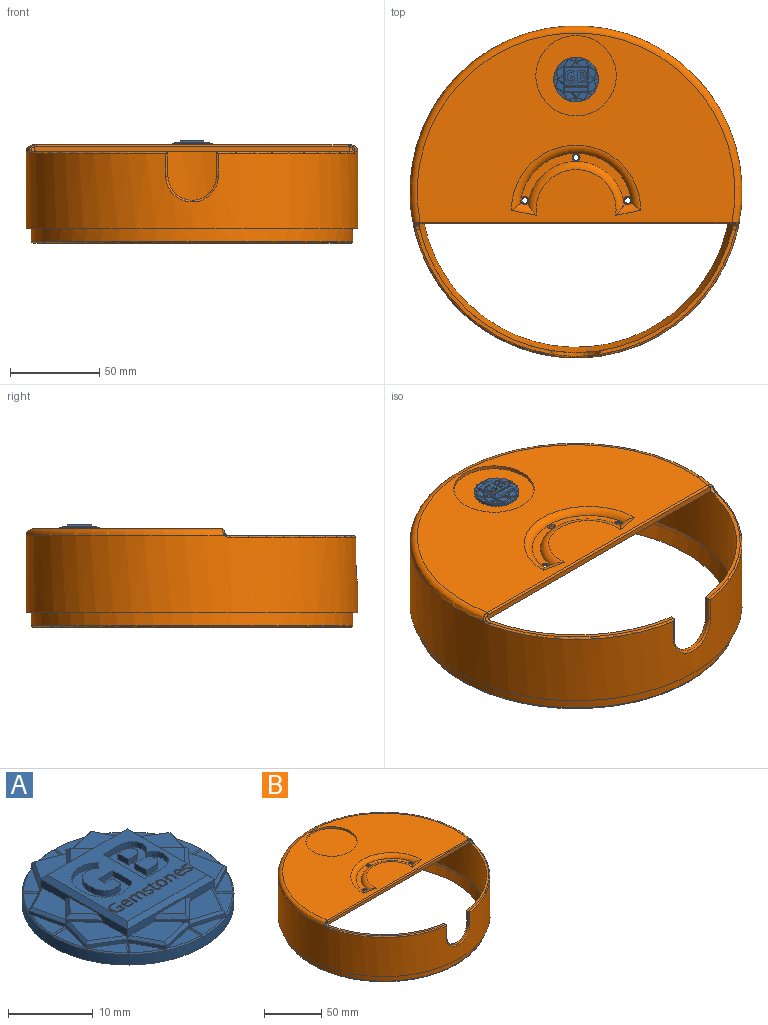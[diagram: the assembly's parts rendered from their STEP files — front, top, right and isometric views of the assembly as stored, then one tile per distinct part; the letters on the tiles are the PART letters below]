
ASSEMBLY  parts=2 mates=1
PART A: 356 faces, bbox 25.1x25.1x4.2 mm
  f0: plane 14.49x1.42mm, normal (0,1,0), area 11.4mm2, adj f11,f13,f15,f320,f322,f339,f340,f341
  f1: cylinder r=12.53mm len=25.05mm, axis (0,0,-1), area 118.3mm2, adj f3,f6,f270,f273,f281,f284,f287,f290
  f2: plane 4.16x4.14mm, normal (0,0,1), area 5.8mm2, adj f3,f4,f8
  f3: cone r=12.36mm half-angle=45deg, axis (0,0,-1), area 1.2mm2, adj f1,f2,f4,f8
  f4: plane 1.74x1.58mm, normal (-0.51,0.49,0.71), area 0.5mm2, adj f2,f3,f7,f8
  f5: plane 3.71x3.26mm, normal (0,0,1), area 4.4mm2, adj f6,f7,f344
  f6: cone r=12.36mm half-angle=45deg, axis (0,0,-1), area 1mm2, adj f1,f5,f7,f344
  f7: plane 1.65x1.65mm, normal (0.51,-0.49,0.71), area 0.5mm2, adj f4,f5,f6,f344
  f8: plane 4.54x2.88mm, normal (0.54,0.84,0), area 2.7mm2, adj f2,f3,f4,f261,f264,f344
  f9: plane 4.32x2.61mm, normal (-0.52,-0.86,0), area 2.6mm2, adj f297,f300,f328,f336,f337,f338
  f10: plane 14.49x1.42mm, normal (0,-1,0), area 11.2mm2, adj f11,f13,f16,f277,f279,f323,f324,f325
  f11: plane 14.55x1.42mm, normal (1,0,0), area 11.1mm2, adj f0,f10,f17,f257,f258,f260,f262,f264
  f12: plane 13.39x13.32mm, normal (0,0,1), area 117.2mm2, adj f14,f15,f16,f17,f18,f19,f20,f21
  f13: plane 14.55x1.42mm, normal (-1,0,0), area 11.1mm2, adj f0,f10,f14,f292,f293,f294,f295,f296
  f14: plane 14.55x0.58mm, normal (-0.71,0,0.71), area 11.5mm2, adj f12,f13,f15,f16
  f15: plane 14.49x0.58mm, normal (0,0.71,0.71), area 11.5mm2, adj f0,f12,f14,f17
  f16: plane 14.49x0.58mm, normal (0,-0.71,0.71), area 11.5mm2, adj f10,f12,f14,f17
  f17: plane 14.55x0.58mm, normal (0.71,0,0.71), area 11.5mm2, adj f11,f12,f15,f16
  f18: extruded ~3.58x3.34mm, area 4.6mm2, adj f12,f19,f31,f32
  f19: extruded ~2.26x0.84mm, area 2.1mm2, adj f12,f18,f20,f32
  f20: plane 3.14x0.84mm, normal (-1,0,0), area 2.6mm2, adj f12,f19,f21,f32
  f21: plane 2.48x0.84mm, normal (0,-1,0), area 2.1mm2, adj f12,f20,f22,f32
  f22: plane 1.14x0.84mm, normal (1,0,0), area 1mm2, adj f12,f21,f23,f32
  f23: plane 1.23x0.84mm, normal (0,1,0), area 1mm2, adj f12,f22,f24,f32
  f24: plane 1.37x0.84mm, normal (1,0,0), area 1.1mm2, adj f12,f23,f25,f32
  f25: extruded ~0.87x0.84mm, area 0.8mm2, adj f12,f24,f26,f32
  f26: extruded ~2.43x2.06mm, area 3mm2, adj f12,f25,f27,f32
  f27: extruded ~2.4x1.97mm, area 2.9mm2, adj f12,f26,f28,f32
  f28: extruded ~1.36x0.84mm, area 1.3mm2, adj f12,f27,f29,f32
  f29: plane 0.88x0.84mm, normal (-0.77,0.64,0), area 1mm2, adj f12,f28,f30,f32
  f30: extruded ~2.15x0.89mm, area 2mm2, adj f12,f29,f31,f32
  f31: extruded ~3.64x3.34mm, area 4.6mm2, adj f12,f18,f30,f32
  f32: plane 7.23x5.6mm, normal (0,0,1), area 21.4mm2, adj f18,f19,f20,f21,f22,f23,f24,f25
  f33: plane 6.96x0.84mm, normal (1,0,0), area 5.8mm2, adj f12,f34,f50,f51
  f34: plane 2.48x0.84mm, normal (0,1,0), area 2.1mm2, adj f12,f33,f35,f51
  f35: extruded ~2.7x2.05mm, area 3.2mm2, adj f12,f34,f36,f51
  f36: extruded ~1.65x1.31mm, area 1.9mm2, adj f12,f35,f37,f51
  f37: plane 0.84x0.05mm, normal (-1,0,0), area 0mm2, adj f12,f36,f38,f51
  f38: extruded ~1.51x0.95mm, area 1.6mm2, adj f12,f37,f39,f51
  f39: extruded ~2.52x1.71mm, area 2.9mm2, adj f12,f38,f50,f51
  f40: plane 0.97x0.84mm, normal (0,-1,0), area 0.8mm2, adj f41,f48,f51,f53
  f41: plane 2.02x0.84mm, normal (-1,0,0), area 1.7mm2, adj f40,f42,f51,f53
  f42: plane 0.97x0.84mm, normal (0,1,0), area 0.8mm2, adj f41,f43,f51,f53
  f43: extruded ~1.47x0.96mm, area 1.7mm2, adj f42,f48,f51,f53
  f44: plane 0.84x0.81mm, normal (0,-1,0), area 0.7mm2, adj f45,f49,f51,f52
  f45: plane 1.77x0.84mm, normal (-1,0,0), area 1.5mm2, adj f44,f46,f51,f52
  f46: plane 0.84x0.83mm, normal (0,1,0), area 0.7mm2, adj f45,f47,f51,f52
  f47: extruded ~1.25x0.86mm, area 1.4mm2, adj f46,f49,f51,f52
  f48: extruded ~1.47x1.06mm, area 1.7mm2, adj f40,f43,f51,f53
  f49: extruded ~1.27x0.91mm, area 1.5mm2, adj f44,f47,f51,f52
  f50: plane 2.3x0.84mm, normal (0,-1,0), area 1.9mm2, adj f12,f33,f39,f51
  f51: plane 6.96x5.18mm, normal (0,0,1), area 24.5mm2, adj f33,f34,f35,f36,f37,f38,f39,f40
  f52: plane 2.08x1.77mm, normal (0,0,1), area 3.3mm2, adj f44,f45,f46,f47,f49
  f53: plane 2.44x2.02mm, normal (0,0,1), area 4.4mm2, adj f40,f41,f42,f43,f48
  f54: extruded ~0.84x0.26mm, area 0.2mm2, adj f55,f72,f73,f252
  f55: extruded ~0.84x0.24mm, area 0.2mm2, adj f54,f56,f73,f252
  f56: extruded ~0.84x0.29mm, area 0.3mm2, adj f55,f57,f73,f252
  f57: plane 0.84x0.7mm, normal (0,-1,0), area 0.6mm2, adj f56,f72,f73,f252
  f58: extruded ~0.84x0.47mm, area 0.4mm2, adj f12,f59,f71,f73
  f59: extruded ~0.84x0.23mm, area 0.2mm2, adj f12,f58,f60,f73
  f60: extruded ~0.84x0.2mm, area 0.2mm2, adj f12,f59,f61,f73
  f61: plane 0.84x0.18mm, normal (-1,0,0), area 0.2mm2, adj f12,f60,f62,f73
  f62: extruded ~0.84x0.43mm, area 0.4mm2, adj f12,f61,f63,f73
  f63: extruded ~0.84x0.32mm, area 0.3mm2, adj f12,f62,f64,f73
  f64: extruded ~0.84x0.36mm, area 0.3mm2, adj f12,f63,f65,f73
  f65: plane 0.92x0.84mm, normal (0,1,0), area 0.8mm2, adj f12,f64,f66,f73
  f66: plane 0.84x0.13mm, normal (-1,0,0), area 0.1mm2, adj f12,f65,f67,f73
  f67: extruded ~0.84x0.44mm, area 0.4mm2, adj f12,f66,f68,f73
  f68: extruded ~0.84x0.4mm, area 0.4mm2, adj f12,f67,f69,f73
  f69: extruded ~0.84x0.43mm, area 0.4mm2, adj f12,f68,f70,f73
  f70: extruded ~0.84x0.51mm, area 0.5mm2, adj f12,f69,f71,f73
  f71: extruded ~0.84x0.5mm, area 0.5mm2, adj f12,f58,f70,f73
  f72: extruded ~0.84x0.29mm, area 0.3mm2, adj f54,f57,f73,f252
  f73: plane 1.39x1.13mm, normal (0,0,1), area 0.7mm2, adj f54,f55,f56,f57,f58,f59,f60,f61
  f74: plane 0.84x0.61mm, normal (0,-1,0), area 0.5mm2, adj f12,f75,f93,f94
  f75: plane 0.84x0.19mm, normal (1,0,0), area 0.2mm2, adj f12,f74,f76,f94
  f76: plane 0.84x0.4mm, normal (0,1,0), area 0.3mm2, adj f12,f75,f77,f94
  f77: plane 0.84x0.55mm, normal (1,0,0), area 0.5mm2, adj f12,f76,f78,f94
  f78: extruded ~0.84x0.36mm, area 0.3mm2, adj f12,f77,f79,f94
  f79: extruded ~0.84x0.52mm, area 0.5mm2, adj f12,f78,f80,f94
  f80: extruded ~0.84x0.55mm, area 0.5mm2, adj f12,f79,f81,f94
  f81: extruded ~0.84x0.54mm, area 0.5mm2, adj f12,f80,f82,f94
  f82: extruded ~0.84x0.51mm, area 0.5mm2, adj f12,f81,f83,f94
  f83: extruded ~0.84x0.46mm, area 0.4mm2, adj f12,f82,f84,f94
  f84: plane 0.84x0.18mm, normal (-0.92,0.4,0), area 0.2mm2, adj f12,f83,f85,f94
  f85: extruded ~0.84x0.53mm, area 0.5mm2, adj f12,f84,f86,f94
  f86: extruded ~0.84x0.49mm, area 0.4mm2, adj f12,f85,f87,f94
  f87: extruded ~0.84x0.32mm, area 0.4mm2, adj f12,f86,f88,f94
  f88: extruded ~0.84x0.49mm, area 0.4mm2, adj f12,f87,f89,f94
  f89: extruded ~0.84x0.67mm, area 0.6mm2, adj f12,f88,f90,f94
  f90: extruded ~0.84x0.63mm, area 0.6mm2, adj f12,f89,f91,f94
  f91: extruded ~0.84x0.34mm, area 0.3mm2, adj f12,f90,f92,f94
  f92: extruded ~0.84x0.29mm, area 0.2mm2, adj f12,f91,f93,f94
  f93: plane 0.87x0.84mm, normal (-1,0,0), area 0.7mm2, adj f12,f74,f92,f94
  f94: plane 1.83x1.48mm, normal (0,0,1), area 1mm2, adj f74,f75,f76,f77,f78,f79,f80,f81
  f95: plane 0.87x0.84mm, normal (1,0,0), area 0.7mm2, adj f12,f96,f122,f123
  f96: plane 0.84x0.2mm, normal (0,1,0), area 0.2mm2, adj f12,f95,f97,f123
  f97: plane 0.87x0.84mm, normal (-1,0,0), area 0.7mm2, adj f12,f96,f98,f123
  f98: extruded ~0.84x0.37mm, area 0.3mm2, adj f12,f97,f99,f123
  f99: extruded ~0.84x0.34mm, area 0.3mm2, adj f12,f98,f100,f123
  f100: extruded ~0.84x0.26mm, area 0.2mm2, adj f12,f99,f101,f123
  f101: extruded ~0.84x0.17mm, area 0.2mm2, adj f12,f100,f102,f123
  f102: plane 0.84x0.01mm, normal (0,-1,0), area 0mm2, adj f12,f101,f103,f123
  f103: extruded ~0.84x0.41mm, area 0.4mm2, adj f12,f102,f104,f123
  f104: extruded ~0.84x0.23mm, area 0.2mm2, adj f12,f103,f105,f123
  f105: extruded ~0.84x0.16mm, area 0.2mm2, adj f12,f104,f106,f123
  f106: plane 0.84x0.01mm, normal (0,-1,0), area 0mm2, adj f12,f105,f107,f123
  f107: plane 0.84x0.18mm, normal (-0.98,-0.18,0), area 0.2mm2, adj f12,f106,f108,f123
  f108: plane 0.84x0.16mm, normal (0,-1,0), area 0.1mm2, adj f12,f107,f109,f123
  f109: plane 1.34x0.84mm, normal (1,0,0), area 1.1mm2, adj f12,f108,f110,f123
  f110: plane 0.84x0.2mm, normal (0,1,0), area 0.2mm2, adj f12,f109,f111,f123
  f111: plane 0.84x0.7mm, normal (-1,0,0), area 0.6mm2, adj f12,f110,f112,f123
  f112: extruded ~0.84x0.37mm, area 0.3mm2, adj f12,f111,f113,f123
  f113: extruded ~0.84x0.28mm, area 0.3mm2, adj f12,f112,f114,f123
  f114: extruded ~0.84x0.21mm, area 0.2mm2, adj f12,f113,f115,f123
  f115: extruded ~0.84x0.24mm, area 0.2mm2, adj f12,f114,f116,f123
  f116: plane 0.87x0.84mm, normal (1,0,0), area 0.7mm2, adj f12,f115,f117,f123
  f117: plane 0.84x0.2mm, normal (0,1,0), area 0.2mm2, adj f12,f116,f118,f123
  f118: plane 0.84x0.75mm, normal (-1,0,0), area 0.6mm2, adj f12,f117,f119,f123
  f119: extruded ~0.84x0.33mm, area 0.3mm2, adj f12,f118,f120,f123
  f120: extruded ~0.84x0.28mm, area 0.3mm2, adj f12,f119,f121,f123
  f121: extruded ~0.84x0.21mm, area 0.2mm2, adj f12,f120,f122,f123
  f122: extruded ~0.84x0.24mm, area 0.2mm2, adj f12,f95,f121,f123
  f123: plane 1.91x1.36mm, normal (0,0,1), area 1mm2, adj f95,f96,f97,f98,f99,f100,f101,f102
  f124: extruded ~0.84x0.29mm, area 0.3mm2, adj f12,f125,f148,f149
  f125: extruded ~0.84x0.22mm, area 0.2mm2, adj f12,f124,f126,f149
  f126: extruded ~0.84x0.32mm, area 0.3mm2, adj f12,f125,f127,f149
  f127: extruded ~0.84x0.23mm, area 0.2mm2, adj f12,f126,f128,f149
  f128: extruded ~0.84x0.09mm, area 0.1mm2, adj f12,f127,f129,f149
  f129: extruded ~0.84x0.09mm, area 0.1mm2, adj f12,f128,f130,f149
  f130: extruded ~0.84x0.12mm, area 0.1mm2, adj f12,f129,f131,f149
  f131: extruded ~0.84x0.22mm, area 0.2mm2, adj f12,f130,f132,f149
  f132: extruded ~0.84x0.36mm, area 0.3mm2, adj f12,f131,f133,f149
  f133: plane 0.84x0.16mm, normal (-0.92,0.4,0), area 0.2mm2, adj f12,f132,f134,f149
  f134: extruded ~0.84x0.42mm, area 0.4mm2, adj f12,f133,f135,f149
  f135: extruded ~0.84x0.36mm, area 0.3mm2, adj f12,f134,f136,f149
  f136: extruded ~0.84x0.26mm, area 0.3mm2, adj f12,f135,f137,f149
  f137: extruded ~0.84x0.16mm, area 0.1mm2, adj f12,f136,f138,f149
  f138: extruded ~0.84x0.12mm, area 0.1mm2, adj f12,f137,f139,f149
  f139: extruded ~0.84x0.27mm, area 0.2mm2, adj f12,f138,f140,f149
  f140: extruded ~0.84x0.26mm, area 0.2mm2, adj f12,f139,f141,f149
  f141: extruded ~0.84x0.13mm, area 0.1mm2, adj f12,f140,f142,f149
  f142: extruded ~0.84x0.15mm, area 0.2mm2, adj f12,f141,f143,f149
  f143: extruded ~0.84x0.24mm, area 0.2mm2, adj f12,f142,f144,f149
  f144: extruded ~0.84x0.21mm, area 0.2mm2, adj f12,f143,f145,f149
  f145: extruded ~0.84x0.21mm, area 0.2mm2, adj f12,f144,f146,f149
  f146: plane 0.84x0.19mm, normal (1,0,0), area 0.2mm2, adj f12,f145,f147,f149
  f147: extruded ~0.84x0.41mm, area 0.4mm2, adj f12,f146,f148,f149
  f148: extruded ~0.84x0.39mm, area 0.3mm2, adj f12,f124,f147,f149
  f149: plane 1.39x0.95mm, normal (0,0,1), area 0.5mm2, adj f124,f125,f126,f127,f128,f129,f130,f131
  f150: extruded ~0.84x0.1mm, area 0.1mm2, adj f12,f151,f168,f169
  f151: extruded ~0.84x0.16mm, area 0.1mm2, adj f12,f150,f152,f169
  f152: extruded ~0.84x0.19mm, area 0.2mm2, adj f12,f151,f153,f169
  f153: plane 0.84x0.79mm, normal (-1,0,0), area 0.7mm2, adj f12,f152,f154,f169
  f154: plane 0.84x0.39mm, normal (0,1,0), area 0.3mm2, adj f12,f153,f155,f169
  f155: plane 0.84x0.16mm, normal (-1,0,0), area 0.1mm2, adj f12,f154,f156,f169
  f156: plane 0.84x0.39mm, normal (0,-1,0), area 0.3mm2, adj f12,f155,f157,f169
  f157: plane 0.84x0.31mm, normal (-1,0,0), area 0.3mm2, adj f12,f156,f158,f169
  f158: plane 0.84x0.12mm, normal (0,-1,0), area 0.1mm2, adj f12,f157,f159,f169
  f159: plane 0.84x0.29mm, normal (0.96,-0.29,0), area 0.2mm2, adj f12,f158,f160,f169
  f160: plane 0.84x0.19mm, normal (0.4,-0.92,0), area 0.2mm2, adj f12,f159,f161,f169
  f161: plane 0.84x0.1mm, normal (1,0,0), area 0.1mm2, adj f12,f160,f162,f169
  f162: plane 0.84x0.19mm, normal (0,1,0), area 0.2mm2, adj f12,f161,f163,f169
  f163: plane 0.84x0.8mm, normal (1,0,0), area 0.7mm2, adj f12,f162,f164,f169
  f164: extruded ~0.84x0.41mm, area 0.5mm2, adj f12,f163,f165,f169
  f165: extruded ~0.84x0.12mm, area 0.1mm2, adj f12,f164,f166,f169
  f166: extruded ~0.84x0.1mm, area 0.1mm2, adj f12,f165,f167,f169
  f167: plane 0.84x0.16mm, normal (-1,0,0), area 0.1mm2, adj f12,f166,f168,f169
  f168: extruded ~0.84x0.08mm, area 0.1mm2, adj f12,f150,f167,f169
  f169: plane 1.67x0.79mm, normal (0,0,1), area 0.5mm2, adj f150,f151,f152,f153,f154,f155,f156,f157
  f170: plane 0.86x0.84mm, normal (1,0,0), area 0.7mm2, adj f12,f171,f186,f187
  f171: plane 0.84x0.2mm, normal (0,1,0), area 0.2mm2, adj f12,f170,f172,f187
  f172: plane 0.87x0.84mm, normal (-1,0,0), area 0.7mm2, adj f12,f171,f173,f187
  f173: extruded ~0.84x0.37mm, area 0.3mm2, adj f12,f172,f174,f187
  f174: extruded ~0.84x0.36mm, area 0.3mm2, adj f12,f173,f175,f187
  f175: extruded ~0.84x0.25mm, area 0.2mm2, adj f12,f174,f176,f187
  f176: extruded ~0.84x0.17mm, area 0.2mm2, adj f12,f175,f177,f187
  f177: plane 0.84x0.01mm, normal (0,-1,0), area 0mm2, adj f12,f176,f178,f187
  f178: plane 0.84x0.18mm, normal (-0.98,-0.18,0), area 0.2mm2, adj f12,f177,f179,f187
  f179: plane 0.84x0.16mm, normal (0,-1,0), area 0.1mm2, adj f12,f178,f180,f187
  f180: plane 1.34x0.84mm, normal (1,0,0), area 1.1mm2, adj f12,f179,f181,f187
  f181: plane 0.84x0.2mm, normal (0,1,0), area 0.2mm2, adj f12,f180,f182,f187
  f182: plane 0.84x0.7mm, normal (-1,0,0), area 0.6mm2, adj f12,f181,f183,f187
  f183: extruded ~0.84x0.37mm, area 0.3mm2, adj f12,f182,f184,f187
  f184: extruded ~0.84x0.31mm, area 0.3mm2, adj f12,f183,f185,f187
  f185: extruded ~0.84x0.23mm, area 0.2mm2, adj f12,f184,f186,f187
  f186: extruded ~0.84x0.24mm, area 0.2mm2, adj f12,f170,f185,f187
  f187: plane 1.36x1.12mm, normal (0,0,1), area 0.6mm2, adj f170,f171,f172,f173,f174,f175,f176,f177
  f188: extruded ~0.84x0.29mm, area 0.3mm2, adj f12,f189,f212,f213
  f189: extruded ~0.84x0.22mm, area 0.2mm2, adj f12,f188,f190,f213
  f190: extruded ~0.84x0.32mm, area 0.3mm2, adj f12,f189,f191,f213
  f191: extruded ~0.84x0.23mm, area 0.2mm2, adj f12,f190,f192,f213
  f192: extruded ~0.84x0.09mm, area 0.1mm2, adj f12,f191,f193,f213
  f193: extruded ~0.84x0.09mm, area 0.1mm2, adj f12,f192,f194,f213
  f194: extruded ~0.84x0.12mm, area 0.1mm2, adj f12,f193,f195,f213
  f195: extruded ~0.84x0.22mm, area 0.2mm2, adj f12,f194,f196,f213
  f196: extruded ~0.84x0.36mm, area 0.3mm2, adj f12,f195,f197,f213
  f197: plane 0.84x0.16mm, normal (-0.92,0.4,0), area 0.2mm2, adj f12,f196,f198,f213
  f198: extruded ~0.84x0.42mm, area 0.4mm2, adj f12,f197,f199,f213
  f199: extruded ~0.84x0.36mm, area 0.3mm2, adj f12,f198,f200,f213
  f200: extruded ~0.84x0.26mm, area 0.3mm2, adj f12,f199,f201,f213
  f201: extruded ~0.84x0.16mm, area 0.1mm2, adj f12,f200,f202,f213
  f202: extruded ~0.84x0.12mm, area 0.1mm2, adj f12,f201,f203,f213
  f203: extruded ~0.84x0.27mm, area 0.2mm2, adj f12,f202,f204,f213
  f204: extruded ~0.84x0.26mm, area 0.2mm2, adj f12,f203,f205,f213
  f205: extruded ~0.84x0.13mm, area 0.1mm2, adj f12,f204,f206,f213
  f206: extruded ~0.84x0.15mm, area 0.2mm2, adj f12,f205,f207,f213
  f207: extruded ~0.84x0.24mm, area 0.2mm2, adj f12,f206,f208,f213
  f208: extruded ~0.84x0.21mm, area 0.2mm2, adj f12,f207,f209,f213
  f209: extruded ~0.84x0.21mm, area 0.2mm2, adj f12,f208,f210,f213
  f210: plane 0.84x0.19mm, normal (1,0,0), area 0.2mm2, adj f12,f209,f211,f213
  f211: extruded ~0.84x0.41mm, area 0.4mm2, adj f12,f210,f212,f213
  f212: extruded ~0.84x0.39mm, area 0.3mm2, adj f12,f188,f211,f213
  f213: plane 1.39x0.95mm, normal (0,0,1), area 0.5mm2, adj f188,f189,f190,f191,f192,f193,f194,f195
  f214: extruded ~0.84x0.26mm, area 0.2mm2, adj f215,f232,f233,f253
  f215: extruded ~0.84x0.24mm, area 0.2mm2, adj f214,f216,f233,f253
  f216: extruded ~0.84x0.29mm, area 0.3mm2, adj f215,f217,f233,f253
  f217: plane 0.84x0.7mm, normal (0,-1,0), area 0.6mm2, adj f216,f232,f233,f253
  f218: extruded ~0.84x0.47mm, area 0.4mm2, adj f12,f219,f231,f233
  f219: extruded ~0.84x0.23mm, area 0.2mm2, adj f12,f218,f220,f233
  f220: extruded ~0.84x0.2mm, area 0.2mm2, adj f12,f219,f221,f233
  f221: plane 0.84x0.18mm, normal (-1,0,0), area 0.2mm2, adj f12,f220,f222,f233
  f222: extruded ~0.84x0.43mm, area 0.4mm2, adj f12,f221,f223,f233
  f223: extruded ~0.84x0.32mm, area 0.3mm2, adj f12,f222,f224,f233
  f224: extruded ~0.84x0.36mm, area 0.3mm2, adj f12,f223,f225,f233
  f225: plane 0.92x0.84mm, normal (0,1,0), area 0.8mm2, adj f12,f224,f226,f233
  f226: plane 0.84x0.13mm, normal (-1,0,0), area 0.1mm2, adj f12,f225,f227,f233
  f227: extruded ~0.84x0.44mm, area 0.4mm2, adj f12,f226,f228,f233
  f228: extruded ~0.84x0.4mm, area 0.4mm2, adj f12,f227,f229,f233
  f229: extruded ~0.84x0.43mm, area 0.4mm2, adj f12,f228,f230,f233
  f230: extruded ~0.84x0.51mm, area 0.5mm2, adj f12,f229,f231,f233
  f231: extruded ~0.84x0.5mm, area 0.5mm2, adj f12,f218,f230,f233
  f232: extruded ~0.84x0.29mm, area 0.3mm2, adj f214,f217,f233,f253
  f233: plane 1.39x1.13mm, normal (0,0,1), area 0.7mm2, adj f214,f215,f216,f217,f218,f219,f220,f221
  f234: extruded ~0.84x0.39mm, area 0.3mm2, adj f235,f250,f251,f254
  f235: extruded ~0.84x0.39mm, area 0.3mm2, adj f234,f236,f251,f254
  f236: extruded ~0.84x0.3mm, area 0.3mm2, adj f235,f237,f251,f254
  f237: extruded ~0.84x0.3mm, area 0.3mm2, adj f236,f238,f251,f254
  f238: extruded ~0.84x0.39mm, area 0.3mm2, adj f237,f239,f251,f254
  f239: extruded ~0.84x0.39mm, area 0.3mm2, adj f238,f240,f251,f254
  f240: extruded ~0.84x0.3mm, area 0.3mm2, adj f239,f250,f251,f254
  f241: extruded ~0.84x0.51mm, area 0.5mm2, adj f12,f242,f249,f251
  f242: extruded ~0.84x0.5mm, area 0.5mm2, adj f12,f241,f243,f251
  f243: extruded ~0.84x0.45mm, area 0.4mm2, adj f12,f242,f244,f251
  f244: extruded ~0.84x0.45mm, area 0.4mm2, adj f12,f243,f245,f251
  f245: extruded ~0.84x0.51mm, area 0.5mm2, adj f12,f244,f246,f251
  f246: extruded ~0.84x0.37mm, area 0.3mm2, adj f12,f245,f247,f251
  f247: extruded ~0.84x0.24mm, area 0.3mm2, adj f12,f246,f248,f251
  f248: extruded ~0.84x0.32mm, area 0.3mm2, adj f12,f247,f249,f251
  f249: extruded ~0.84x0.45mm, area 0.4mm2, adj f12,f241,f248,f251
  f250: extruded ~0.84x0.3mm, area 0.3mm2, adj f234,f240,f251,f254
  f251: plane 1.39x1.23mm, normal (0,0,1), area 0.7mm2, adj f234,f235,f236,f237,f238,f239,f240,f241
  f252: plane 0.7x0.39mm, normal (0,0,1), area 0.2mm2, adj f54,f55,f56,f57,f72
  f253: plane 0.7x0.39mm, normal (0,0,1), area 0.2mm2, adj f214,f215,f216,f217,f232
  f254: plane 1.04x0.81mm, normal (0,0,1), area 0.7mm2, adj f234,f235,f236,f237,f238,f239,f240,f250
  f255: plane 4.27x2.15mm, normal (0.45,-0.89,0), area 2.4mm2, adj f256,f258,f275,f289,f290,f291
  f256: plane 5.21x1.18mm, normal (0.98,0.22,0), area 2.7mm2, adj f255,f259,f261,f272,f273,f274
  f257: plane 6.7x3.88mm, normal (0,0,1), area 15.6mm2, adj f11,f258,f259,f260
  f258: plane 4.27x2.33mm, normal (0.32,-0.63,0.71), area 2.2mm2, adj f11,f255,f257,f259
  f259: plane 5.21x1.46mm, normal (0.69,0.16,0.71), area 2.4mm2, adj f256,f257,f258,f260
  f260: plane 3.17x3.09mm, normal (0.72,-0.7,0), area 1.5mm2, adj f11,f257,f259,f265,f267
  f261: plane 4.33x1.45mm, normal (0.95,-0.32,0), area 2.3mm2, adj f8,f256,f263,f269,f270,f271
  f262: plane 6.55x4.14mm, normal (0,0,1), area 15.2mm2, adj f11,f263,f264,f265
  f263: plane 4.32x1.72mm, normal (0.67,-0.22,0.71), area 2.1mm2, adj f261,f262,f264,f265
  f264: plane 4.54x3.02mm, normal (0.38,0.6,0.71), area 2.4mm2, adj f8,f11,f262,f263
  f265: plane 3.09x3.01mm, normal (0.7,0.72,0), area 1.5mm2, adj f11,f260,f262,f263,f268
  f266: plane 4.76x2.38mm, normal (0,0,1), area 5.7mm2, adj f11,f267,f268
  f267: plane 3.17x3.09mm, normal (0.51,-0.49,0.71), area 2.8mm2, adj f11,f260,f266,f268
  f268: plane 3.09x3.02mm, normal (0.49,0.51,0.71), area 2.7mm2, adj f11,f265,f266,f267
  f269: plane 4.01x2.04mm, normal (0,0,1), area 4.5mm2, adj f261,f270,f271
  f270: cone r=12.36mm half-angle=45deg, axis (0,0,-1), area 1mm2, adj f1,f261,f269,f271
  f271: plane 2.26x0.28mm, normal (-0.03,-0.71,0.71), area 0.5mm2, adj f261,f269,f270,f274
  f272: plane 4.76x2.06mm, normal (0,0,1), area 5.6mm2, adj f256,f273,f274
  f273: cone r=12.36mm half-angle=45deg, axis (0,0,-1), area 1.2mm2, adj f1,f256,f272,f274
  f274: plane 2.26x0.27mm, normal (0.03,0.71,0.71), area 0.5mm2, adj f256,f271,f272,f273
  f275: plane 4.42x2.6mm, normal (0.86,-0.51,0), area 2.6mm2, adj f255,f276,f279,f286,f287,f288
  f276: plane 4.62x1.4mm, normal (-0.29,-0.96,0), area 2.5mm2, adj f275,f278,f283,f284,f285,f329
  f277: plane 6.54x4.02mm, normal (0,0,1), area 14.9mm2, adj f10,f278,f279,f326
  f278: plane 4.61x1.66mm, normal (-0.2,-0.68,0.71), area 2.2mm2, adj f276,f277,f279,f326
  f279: plane 4.42x2.75mm, normal (0.61,-0.36,0.71), area 2.3mm2, adj f10,f275,f277,f278
  f280: plane 4.65x2.05mm, normal (0,0,1), area 5.5mm2, adj f281,f282,f329
  f281: cone r=12.36mm half-angle=45deg, axis (0,0,-1), area 1.2mm2, adj f1,f280,f282,f329
  f282: plane 2.26x0.2mm, normal (0.71,0.01,0.71), area 0.5mm2, adj f280,f281,f285,f329
  f283: plane 4.18x2.04mm, normal (0,0,1), area 4.8mm2, adj f276,f284,f285
  f284: cone r=12.36mm half-angle=45deg, axis (0,0,-1), area 1.1mm2, adj f1,f276,f283,f285
  f285: plane 2.26x0.2mm, normal (-0.71,-0.01,0.71), area 0.5mm2, adj f276,f282,f283,f284
  f286: plane 4.03x3.9mm, normal (0,0,1), area 5.5mm2, adj f275,f287,f288
  f287: cone r=12.36mm half-angle=45deg, axis (0,0,-1), area 1.2mm2, adj f1,f275,f286,f288
  f288: plane 1.77x1.62mm, normal (0.49,0.51,0.71), area 0.5mm2, adj f275,f286,f287,f291
  f289: plane 3.87x3.41mm, normal (0,0,1), area 4.8mm2, adj f255,f290,f291
  f290: cone r=12.36mm half-angle=45deg, axis (0,0,-1), area 1mm2, adj f1,f255,f289,f291
  f291: plane 1.7x1.68mm, normal (-0.49,-0.51,0.71), area 0.5mm2, adj f255,f288,f289,f290
  f292: plane 3.02x2.95mm, normal (-0.71,0.7,0), area 1.5mm2, adj f13,f293,f295,f309,f311
  f293: plane 3.19x2.95mm, normal (-0.73,-0.68,0), area 1.5mm2, adj f13,f292,f296,f298,f299
  f294: plane 4.75x2.26mm, normal (0,0,1), area 5.4mm2, adj f13,f295,f296
  f295: plane 3.03x2.95mm, normal (-0.51,0.49,0.71), area 2.6mm2, adj f13,f292,f294,f296
  f296: plane 3.19x2.95mm, normal (-0.52,-0.48,0.71), area 2.7mm2, adj f13,f293,f294,f295
  f297: plane 4.75x1.37mm, normal (-0.96,0.28,0), area 2.5mm2, adj f9,f299,f308,f315,f316,f317
  f298: plane 6.68x3.93mm, normal (0,0,1), area 15mm2, adj f13,f293,f299,f300
  f299: plane 4.75x1.64mm, normal (-0.68,0.2,0.71), area 2.2mm2, adj f293,f297,f298,f300
  f300: plane 4.32x2.76mm, normal (-0.36,-0.61,0.71), area 2.3mm2, adj f9,f13,f298,f299
  f301: plane 4.16x4.05mm, normal (0,0,1), area 5.6mm2, adj f302,f303,f319
  f302: cone r=12.36mm half-angle=45deg, axis (0,0,-1), area 1.2mm2, adj f1,f301,f303,f319
  f303: plane 1.71x1.48mm, normal (-0.48,-0.52,0.71), area 0.5mm2, adj f301,f302,f306,f319
  f304: plane 3.71x3.29mm, normal (0,0,1), area 4.3mm2, adj f305,f306,f307
  f305: cone r=12.36mm half-angle=45deg, axis (0,0,-1), area 1mm2, adj f1,f304,f306,f307
  f306: plane 1.62x1.56mm, normal (0.48,0.52,0.71), area 0.5mm2, adj f303,f304,f305,f307
  f307: plane 4.11x2.17mm, normal (-0.47,0.88,0), area 2.4mm2, adj f304,f305,f306,f308,f310,f319
  f308: plane 5.03x1.16mm, normal (-0.97,-0.22,0), area 2.6mm2, adj f297,f307,f311,f312,f313,f314
  f309: plane 6.54x3.73mm, normal (0,0,1), area 14.6mm2, adj f13,f292,f310,f311
  f310: plane 4.11x2.35mm, normal (-0.33,0.63,0.71), area 2.1mm2, adj f13,f307,f309,f311
  f311: plane 5.03x1.44mm, normal (-0.69,-0.16,0.71), area 2.3mm2, adj f292,f308,f309,f310
  f312: plane 4.59x2.05mm, normal (0,0,1), area 5.4mm2, adj f308,f313,f314
  f313: cone r=12.36mm half-angle=45deg, axis (0,0,-1), area 1.2mm2, adj f1,f308,f312,f314
  f314: plane 2.26x0.17mm, normal (0,-0.71,0.71), area 0.5mm2, adj f308,f312,f313,f317
  f315: plane 4.32x2.05mm, normal (0,0,1), area 5mm2, adj f297,f316,f317
  f316: cone r=12.36mm half-angle=45deg, axis (0,0,-1), area 1.1mm2, adj f1,f297,f315,f317
  f317: plane 2.26x0.17mm, normal (0,0.71,0.71), area 0.5mm2, adj f297,f314,f315,f316
  f318: plane 4.19x1.55mm, normal (0.35,0.94,0), area 2.3mm2, adj f319,f321,f348,f349,f350,f351
  f319: plane 4.43x2.95mm, normal (-0.83,0.55,0), area 2.7mm2, adj f301,f302,f303,f307,f318,f322
  f320: plane 6.49x4.02mm, normal (0,0,1), area 14.8mm2, adj f0,f321,f322,f343
  f321: plane 4.19x1.81mm, normal (0.24,0.66,0.71), area 2mm2, adj f318,f320,f322,f343
  f322: plane 4.43x3.08mm, normal (-0.59,0.39,0.71), area 2.4mm2, adj f0,f319,f320,f321
  f323: plane 3.16x3.02mm, normal (0.49,-0.51,0.71), area 2.7mm2, adj f10,f324,f325,f326
  f324: plane 3.02x2.91mm, normal (-0.51,-0.49,0.71), area 2.6mm2, adj f10,f323,f325,f327
  f325: plane 4.63x2.31mm, normal (0,0,1), area 5.4mm2, adj f10,f323,f324
  f326: plane 3.16x3.02mm, normal (0.69,-0.72,0), area 1.5mm2, adj f10,f277,f278,f323,f327
  f327: plane 3.02x2.89mm, normal (-0.72,-0.69,0), area 1.5mm2, adj f10,f324,f326,f330,f332
  f328: plane 4.2x2.22mm, normal (-0.88,-0.47,0), area 2.4mm2, adj f9,f329,f331,f333,f334,f335
  f329: plane 5.06x1.18mm, normal (0.23,-0.97,0), area 2.6mm2, adj f276,f280,f281,f282,f328,f332
  f330: plane 6.63x3.81mm, normal (0,0,1), area 15.4mm2, adj f10,f327,f331,f332
  f331: plane 4.2x2.39mm, normal (-0.63,-0.33,0.71), area 2.1mm2, adj f10,f328,f330,f332
  f332: plane 5.06x1.46mm, normal (0.16,-0.69,0.71), area 2.3mm2, adj f327,f329,f330,f331
  f333: plane 3.8x3.33mm, normal (0,0,1), area 4.5mm2, adj f328,f334,f335
  f334: cone r=12.36mm half-angle=45deg, axis (0,0,-1), area 1mm2, adj f1,f328,f333,f335
  f335: plane 1.69x1.56mm, normal (-0.53,0.46,0.71), area 0.5mm2, adj f328,f333,f334,f338
  f336: plane 3.94x3.9mm, normal (0,0,1), area 5.3mm2, adj f9,f337,f338
  f337: cone r=12.36mm half-angle=45deg, axis (0,0,-1), area 1.2mm2, adj f1,f9,f336,f338
  f338: plane 1.77x1.48mm, normal (0.53,-0.46,0.71), area 0.5mm2, adj f9,f335,f336,f337
  f339: plane 2.88x2.76mm, normal (-0.51,0.49,0.71), area 2.5mm2, adj f0,f340,f341,f343
  f340: plane 3.03x2.88mm, normal (0.49,0.51,0.71), area 2.6mm2, adj f0,f339,f341,f342
  f341: plane 4.36x2.18mm, normal (0,0,1), area 4.7mm2, adj f0,f339,f340
  f342: plane 3.03x2.88mm, normal (0.69,0.72,0), area 1.5mm2, adj f0,f340,f343,f352,f354
  f343: plane 2.88x2.75mm, normal (-0.72,0.69,0), area 1.4mm2, adj f0,f320,f321,f339,f342
  f344: plane 4.11x2.04mm, normal (0.9,0.44,0), area 2.3mm2, adj f5,f6,f7,f8,f351,f353
  f345: plane 4.87x2.12mm, normal (0,0,1), area 5.8mm2, adj f346,f347,f351
  f346: cone r=12.36mm half-angle=45deg, axis (0,0,-1), area 1.2mm2, adj f1,f345,f347,f351
  f347: plane 2.33x0.33mm, normal (-0.71,0.05,0.71), area 0.5mm2, adj f345,f346,f350,f351
  f348: plane 3.94x2.1mm, normal (0,0,1), area 4.5mm2, adj f318,f349,f350
  f349: cone r=12.36mm half-angle=45deg, axis (0,0,-1), area 1mm2, adj f1,f318,f348,f350
  f350: plane 2.33x0.34mm, normal (0.71,-0.05,0.71), area 0.5mm2, adj f318,f347,f348,f349
  f351: plane 5.31x1.23mm, normal (-0.23,0.97,0), area 2.8mm2, adj f318,f344,f345,f346,f347,f354
  f352: plane 6.68x3.73mm, normal (0,0,1), area 15.2mm2, adj f0,f342,f353,f354
  f353: plane 4.11x2.22mm, normal (0.63,0.31,0.71), area 2.1mm2, adj f0,f344,f352,f354
  f354: plane 5.31x1.5mm, normal (-0.16,0.69,0.71), area 2.5mm2, adj f342,f351,f352,f353
  f355: plane 25.05x25.05mm, normal (0,0,-1), area 492.8mm2, adj f1
PART B: 41 faces, bbox 201.3x200.2x55 mm
  f0: plane 76.07x70mm, normal (0,0,1), area 216.4mm2, adj f17,f26,f30,f32,f34
  f1: plane 76.07x70mm, normal (0,0,1), area 216.4mm2, adj f17,f27,f29,f33,f35
  f2: cylinder r=93mm len=186mm, axis (0,0,1), area 24171.6mm2, adj f6,f25,f31,f32,f33,f34,f35,f36
  f3: plane 178x106mm, normal (0,0,1), area 12548.3mm2, adj f10,f11,f12,f13,f14,f25,f40
  f4: plane 178x178mm, normal (0,0,-1), area 1105.8mm2, adj f7,f18
  f5: cylinder r=90mm len=180mm, axis (0,0,-1), area 3958.4mm2, adj f6,f7
  f6: plane 186x186mm, normal (0,0,-1), area 1724.7mm2, adj f2,f5
  f7: torus R=89mm, axis (0,0,1), area 884.7mm2, adj f4,f5
  f8: plane 45x45mm, normal (0,0,1), area 1590.4mm2, adj f10
  f9: plane 62.76x29.13mm, normal (0,0,1), area 347.2mm2, adj f11,f12,f13,f14,f22,f23,f24
  f10: cylinder r=22.5mm len=45mm, axis (0,0,1), area 282.7mm2, adj f3,f8
  f11: torus R=22.42mm, axis (0,0,-1), area 462.1mm2, adj f3,f9,f12,f14
  f12: cylinder r=5mm len=14.87mm, axis (-0.98,-0.2,0), area 54.5mm2, adj f3,f9,f11,f13
  f13: torus R=36.14mm, axis (0,0,1), area 592.8mm2, adj f3,f9,f12,f14
  f14: cylinder r=5mm len=14.87mm, axis (0.98,-0.2,0), area 54.5mm2, adj f3,f9,f11,f13
  f15: plane 176.38x3.01mm, normal (0,-1,0), area 529.1mm2, adj f16,f17,f38,f39,f40
  f16: plane 180x108mm, normal (0,0,-1), area 15917.6mm2, adj f15,f17,f19,f20,f21
  f17: cylinder r=90mm len=180mm, axis (0,0,1), area 22536mm2, adj f0,f1,f15,f16,f18,f26,f27,f28
  f18: cone r=90mm half-angle=16.7deg, axis (0,0,1), area 5805.5mm2, adj f4,f17
  f19: cylinder r=1.6mm len=3.2mm, axis (0,0,1), area 4mm2, adj f16,f22
  f20: cylinder r=1.6mm len=3.2mm, axis (0,0,1), area 4mm2, adj f16,f24
  f21: cylinder r=1.6mm len=3.2mm, axis (0,0,1), area 4mm2, adj f16,f23
  f22: cone r=1.6mm half-angle=45deg, axis (0,0,1), area 10.1mm2, adj f9,f19
  f23: cone r=1.6mm half-angle=45deg, axis (0,0,1), area 10.1mm2, adj f9,f21
  f24: cone r=1.6mm half-angle=45deg, axis (0,0,1), area 10.1mm2, adj f9,f20
  f25: torus R=89mm, axis (0,0,1), area 2027mm2, adj f2,f3,f38,f39
  f26: plane 13.5x1.87mm, normal (1,0,0), area 25.2mm2, adj f0,f17,f28,f32
  f27: plane 13.5x1.87mm, normal (-1,0,0), area 25.2mm2, adj f1,f17,f28,f33
  f28: cylinder r=13.5mm len=27mm, axis (0,-1,0), area 82mm2, adj f17,f26,f27,f31
  f29: cylinder r=3mm len=3mm, axis (-1,0,0), area 7.6mm2, adj f1,f17,f37,f39
  f30: cylinder r=3mm len=3mm, axis (-1,0,0), area 7.6mm2, adj f0,f17,f36,f38
  f31: bspline ~29.32x16.12mm, area 72.1mm2, adj f2,f28,f32,f33
  f32: cylinder r=1mm len=13.5mm, axis (0,0,1), area 22.8mm2, adj f0,f2,f26,f31,f34
  f33: cylinder r=1mm len=13.5mm, axis (0,0,1), area 22.8mm2, adj f1,f2,f27,f31,f35
  f34: torus R=92mm, axis (0,0,1), area 172.8mm2, adj f0,f2,f32,f36
  f35: torus R=92mm, axis (0,0,1), area 172.8mm2, adj f1,f2,f33,f37
  f36: bspline ~4.14x2.17mm, area 3.8mm2, adj f2,f30,f34,f38
  f37: bspline ~4.14x2.17mm, area 3.8mm2, adj f2,f29,f35,f39
  f38: bspline ~4.47x4.23mm, area 7.5mm2, adj f15,f17,f25,f30,f36,f40
  f39: bspline ~4.6x4.22mm, area 7.5mm2, adj f15,f17,f25,f29,f37,f40
  f40: cylinder r=1mm len=174.72mm, axis (1,0,0), area 274.5mm2, adj f3,f15,f38,f39
PLACE A t=(1.88,66.55,28.86)mm
PLACE B t=(1.88,3.66,-24.14)mm
MATE parallel A.f1 <-> B.f3  axis (0,0,-1) through (1.88,66.55,28.86)mm
